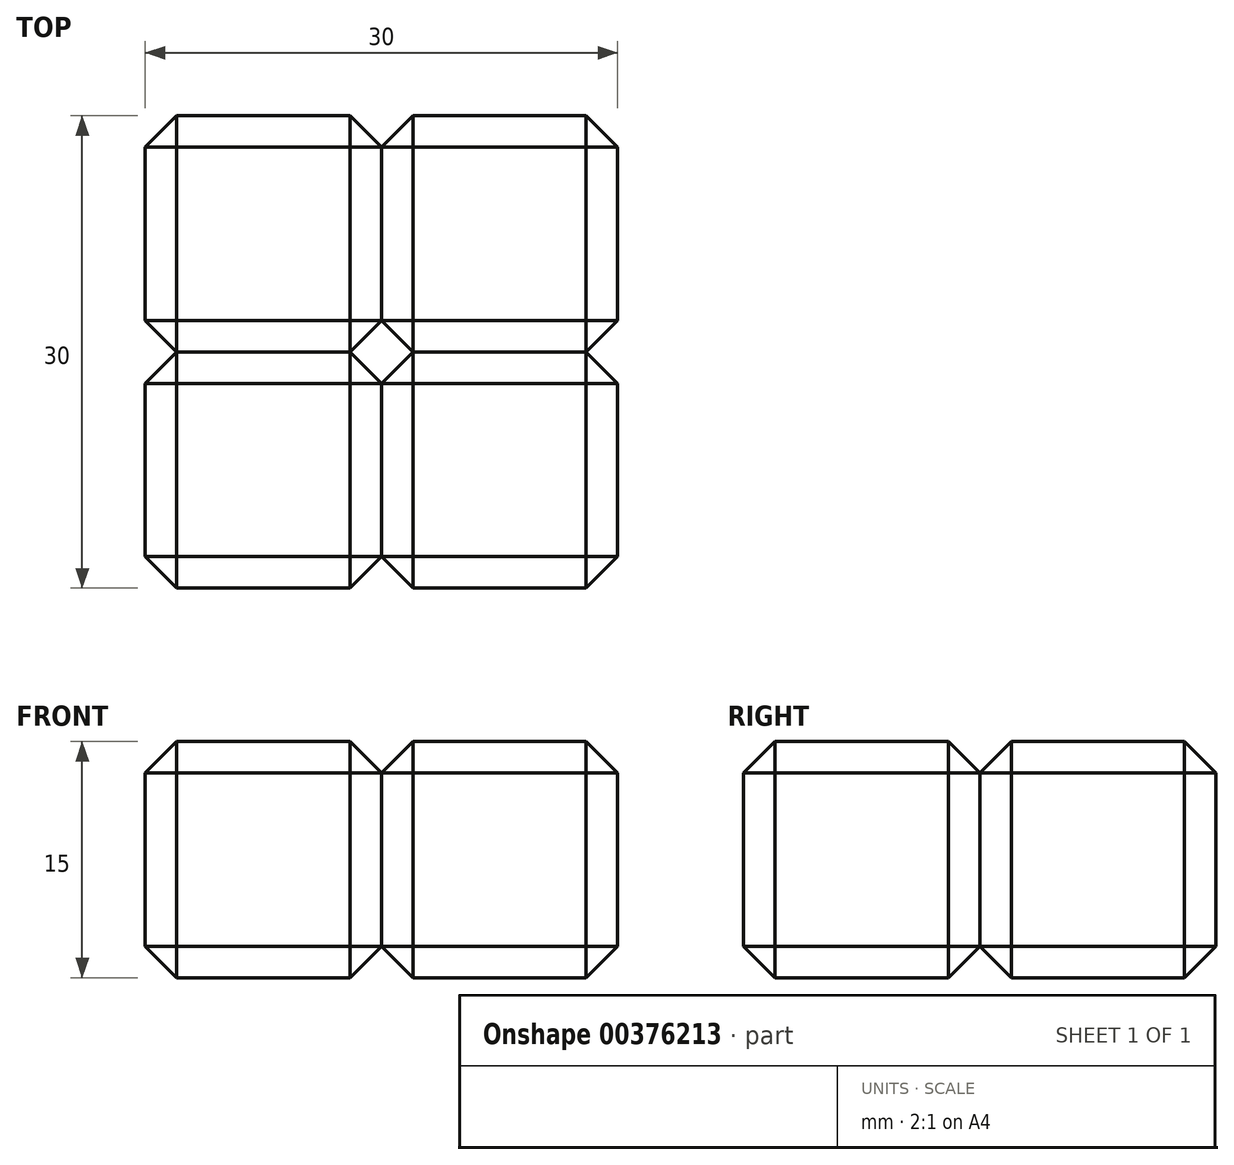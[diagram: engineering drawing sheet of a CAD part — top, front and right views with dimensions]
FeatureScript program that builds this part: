
annotation { "Feature Type Name" : "Feature", "Feature Type Description" : "" }
export const myFeature = defineFeature(function(context is Context, id is Id, definition is map)
    precondition{}
    {
        {
            var Q0;
            Q0=qCreatedBy(makeId("Front.planeOp"),FACE);
            var sketch = newSketch(context, id + "F0", { "sketchPlane" : qUnion([Q0])});
            skLineSegment(sketch, "E0.bottom", {"start": v(7.5, 7.5) * mm, "end": v(-7.5, 7.5) * mm});
            skLineSegment(sketch, "E0.top", {"start": v(7.5, -7.5) * mm, "end": v(-7.5, -7.5) * mm});
            skLineSegment(sketch, "E0.left", {"start": v(7.5, 7.5) * mm, "end": v(7.5, -7.5) * mm});
            skLineSegment(sketch, "E0.right", {"start": v(-7.5, 7.5) * mm, "end": v(-7.5, -7.5) * mm});
            skPoint(sketch, "E0.middle", {"position": v(0, 0) * mm});
            skSolve(sketch);
        }
        {
            var Q0;
            Q0 = qSketchRegion(id + "F0", true);
            extrude(context, id + "F1", {"entities" : qUnion([Q0]), "depth" : 15 * mm});
        }
        {
            var Q0;
            Q0=makeQuery(id+"F1.opExtrude","SWEPT_FACE",FACE,{"disambiguationData":[OSD([sQuery(id+"F0.wireOp",EDGE,"E0.bottom")])]});
            var Q1;
            Q1=makeQuery(id+"F1.opExtrude","CAP_FACE",FACE,{"disambiguationData":[OSD([sQuery(id+"F0.wireOp",EDGE,"E0.bottom"),sQuery(id+"F0.wireOp",EDGE,"E0.top"),sQuery(id+"F0.wireOp",EDGE,"E0.left"),sQuery(id+"F0.wireOp",EDGE,"E0.right")])],"isStart":false});
            var Q2;
            Q2=makeQuery(id+"F1.opExtrude","SWEPT_FACE",FACE,{"disambiguationData":[OSD([sQuery(id+"F0.wireOp",EDGE,"E0.right")])]});
            var Q3;
            Q3=makeQuery(id+"F1.opExtrude","CAP_EDGE",EDGE,{"disambiguationData":[OSD([sQuery(id+"F0.wireOp",EDGE,"E0.top")])],"isStart":true});
            var Q4;
            Q4=makeQuery(id+"F1.opExtrude","SWEPT_FACE",FACE,{"disambiguationData":[OSD([sQuery(id+"F0.wireOp",EDGE,"E0.left")])]});
            chamfer(context, id + "F2", {"entities" : qUnion([Q0, Q1, Q2, Q3, Q4]), "width" : 2 * mm, "tangentPropagation" : true});
        }
        {
            var Q0;
            Q0=makeQuery(id+"F1.opExtrude","SWEPT_BODY",BODY,{"disambiguationData":[OSD([sQuery(id+"F0.wireOp",EDGE,"E0.bottom"),sQuery(id+"F0.wireOp",EDGE,"E0.top"),sQuery(id+"F0.wireOp",EDGE,"E0.left"),sQuery(id+"F0.wireOp",EDGE,"E0.right")])]});
            transform(context, id + "F3", {"entities" : qUnion([Q0]), "transformType" : TransformType.TRANSLATION_3D, "dx" : 15 * mm, "dy" : 0 * mm, "dz" : 0 * mm, "makeCopy" : true});
        }
        {
            var Q0;
            Q0=makeQuery(id+"F3.opPattern","COPY",BODY,{"derivedFrom":makeQuery(id+"F1.opExtrude","SWEPT_BODY",BODY,{"disambiguationData":[OSD([sQuery(id+"F0.wireOp",EDGE,"E0.bottom"),sQuery(id+"F0.wireOp",EDGE,"E0.top"),sQuery(id+"F0.wireOp",EDGE,"E0.left"),sQuery(id+"F0.wireOp",EDGE,"E0.right")])]}),"instanceName":"1"});
            transform(context, id + "F4", {"entities" : qUnion([Q0]), "transformType" : TransformType.TRANSLATION_3D, "dx" : 0 * mm, "dy" : 15 * mm, "dz" : 0 * mm, "makeCopy" : true});
        }
        {
            var Q0;
            Q0=makeQuery(id+"F1.opExtrude","SWEPT_BODY",BODY,{"disambiguationData":[OSD([sQuery(id+"F0.wireOp",EDGE,"E0.bottom"),sQuery(id+"F0.wireOp",EDGE,"E0.top"),sQuery(id+"F0.wireOp",EDGE,"E0.left"),sQuery(id+"F0.wireOp",EDGE,"E0.right")])]});
            transform(context, id + "F5", {"entities" : qUnion([Q0]), "transformType" : TransformType.TRANSLATION_3D, "dx" : 0 * mm, "dy" : 15 * mm, "dz" : 0 * mm, "makeCopy" : true});
        }
    });
